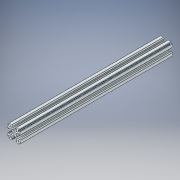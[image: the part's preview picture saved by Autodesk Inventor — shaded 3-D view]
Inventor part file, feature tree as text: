
AUTODESK INVENTOR PART (.ipt)
format: ipt  version: 2017 (Build 210142000, 142)  size: 299,008 bytes
history: native  units: in
note: dims shown in document units (in); Inventor stores cm internally (conversion verified against a paired STEP export)
features: extrude x1, sketch x1, fillet x1
ambient origin geometry x8: Origin, YZ Plane, XZ Plane, XY Plane, X Axis, Y Axis, Z Axis, Center Point
bodies: Solid1 (feature_tree)
feature tree (3):
  extrude  "Extrusion1"  [1 undecoded]
  sketch  "Sketch2"  dims[d0=60.5in d1=0.0in]
  fillet  "Fillet10"  [1 undecoded]
note: 2 required parameter values undecoded (feature->parameter linkage not recoverable at this tier; creation-order binding heuristic only, values carry confidence <= 0.55)
